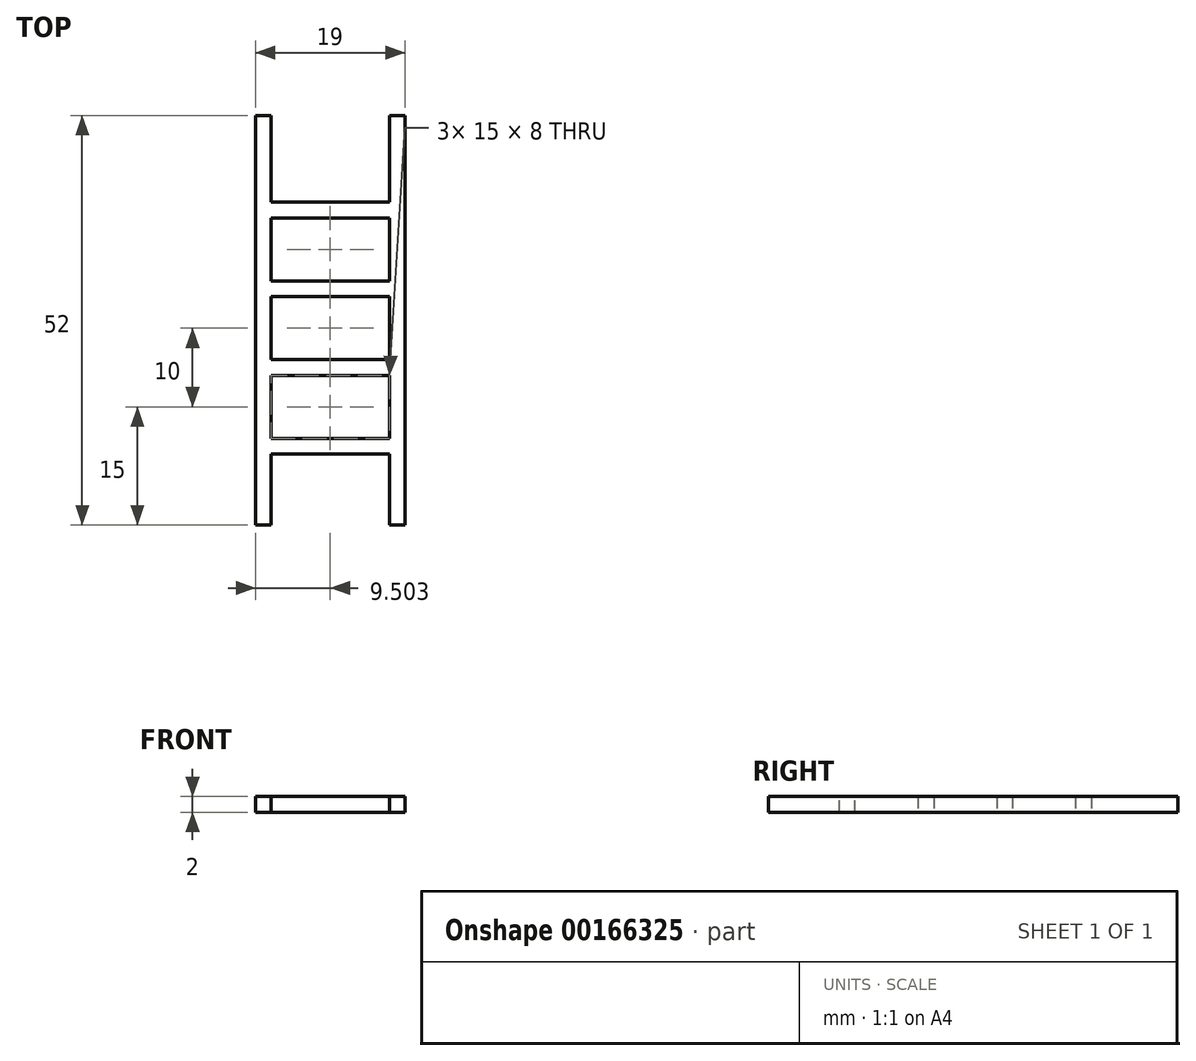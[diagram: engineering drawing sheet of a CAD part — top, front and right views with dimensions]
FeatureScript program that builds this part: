
annotation { "Feature Type Name" : "Feature", "Feature Type Description" : "" }
export const myFeature = defineFeature(function(context is Context, id is Id, definition is map)
    precondition{}
    {
        {
            var Q0;
            Q0=qCreatedBy(makeId("Front.planeOp"),FACE);
            var sketch = newSketch(context, id + "F0", { "sketchPlane" : qUnion([Q0])});
            skLineSegment(sketch, "E0.bottom", {"start": v(-30.22, 16.27) * mm, "end": v(-28.22, 16.27) * mm});
            skLineSegment(sketch, "E0.top", {"start": v(-30.22, 14.27) * mm, "end": v(-28.22, 14.27) * mm});
            skLineSegment(sketch, "E0.left", {"start": v(-30.22, 16.27) * mm, "end": v(-30.22, 14.27) * mm});
            skLineSegment(sketch, "E0.right", {"start": v(-28.22, 16.27) * mm, "end": v(-28.22, 14.27) * mm});
            skLineSegment(sketch, "E1.bottom", {"start": v(-13.22, 16.27) * mm, "end": v(-11.22, 16.27) * mm});
            skLineSegment(sketch, "E1.top", {"start": v(-13.22, 14.27) * mm, "end": v(-11.22, 14.27) * mm});
            skLineSegment(sketch, "E1.left", {"start": v(-13.22, 16.27) * mm, "end": v(-13.22, 14.27) * mm});
            skLineSegment(sketch, "E1.right", {"start": v(-11.22, 16.27) * mm, "end": v(-11.22, 14.27) * mm});
            skPoint(sketch, "E1.middle", {"position": v(-12.22, 15.27) * mm});
            skPoint(sketch, "E1.middle.positionSnap0", {"position": v(-28.22, 15.27) * mm});
            skPoint(sketch, "E1.centerSnap0", {"position": v(-28.22, 15.27) * mm});
            skSolve(sketch);
        }
        {
            var Q0;
            Q0=qSketchRegion(id+"F0",true);
            extrude(context, id + "F1", {"entities" : qUnion([Q0]), "depth" : 52 * mm});
        }
        {
            var Q0;
            Q0=makeQuery(id+"F1.opExtrude","SWEPT_FACE",FACE,{"disambiguationData":[OSD([sQuery(id+"F0.wireOp",EDGE,"E0.right")])]});
            var sketch = newSketch(context, id + "F2", { "sketchPlane" : qUnion([Q0])});
            skLineSegment(sketch, "E2.bottom", {"start": v(-41, 14.27) * mm, "end": v(-43, 14.27) * mm});
            skLineSegment(sketch, "E2.top", {"start": v(-41, 16.27) * mm, "end": v(-43, 16.27) * mm});
            skLineSegment(sketch, "E2.left", {"start": v(-41, 14.27) * mm, "end": v(-41, 16.27) * mm});
            skLineSegment(sketch, "E2.right", {"start": v(-43, 14.27) * mm, "end": v(-43, 16.27) * mm});
            skPoint(sketch, "E2.middle", {"position": v(-42, 15.27) * mm});
            skPoint(sketch, "E2.middle.positionSnap0", {"position": v(-52, 15.27) * mm});
            skPoint(sketch, "E2.centerSnap0", {"position": v(-52, 15.27) * mm});
            skLineSegment(sketch, "E3.bottom", {"start": v(-33, 16.27) * mm, "end": v(-31, 16.27) * mm});
            skLineSegment(sketch, "E3.top", {"start": v(-33, 14.27) * mm, "end": v(-31, 14.27) * mm});
            skLineSegment(sketch, "E3.left", {"start": v(-33, 16.27) * mm, "end": v(-33, 14.27) * mm});
            skLineSegment(sketch, "E3.right", {"start": v(-31, 16.27) * mm, "end": v(-31, 14.27) * mm});
            skPoint(sketch, "E3.middle", {"position": v(-32, 15.27) * mm});
            skPoint(sketch, "E3.middle.positionSnap0", {"position": v(-41, 15.27) * mm});
            skPoint(sketch, "E3.centerSnap0", {"position": v(-41, 15.27) * mm});
            skLineSegment(sketch, "E4.bottom", {"start": v(-23, 16.27) * mm, "end": v(-21, 16.27) * mm});
            skLineSegment(sketch, "E4.top", {"start": v(-23, 14.27) * mm, "end": v(-21, 14.27) * mm});
            skLineSegment(sketch, "E4.left", {"start": v(-23, 16.27) * mm, "end": v(-23, 14.27) * mm});
            skLineSegment(sketch, "E4.right", {"start": v(-21, 16.27) * mm, "end": v(-21, 14.27) * mm});
            skPoint(sketch, "E4.middle", {"position": v(-22, 15.27) * mm});
            skLineSegment(sketch, "E5.bottom", {"start": v(-13, 16.27) * mm, "end": v(-11, 16.27) * mm});
            skLineSegment(sketch, "E5.top", {"start": v(-13, 14.27) * mm, "end": v(-11, 14.27) * mm});
            skLineSegment(sketch, "E5.left", {"start": v(-13, 16.27) * mm, "end": v(-13, 14.27) * mm});
            skLineSegment(sketch, "E5.right", {"start": v(-11, 16.27) * mm, "end": v(-11, 14.27) * mm});
            skPoint(sketch, "E5.middle", {"position": v(-12, 15.27) * mm});
            skLineSegment(sketch, "E6.bottom", {"start": v(-11, 16.27) * mm, "end": v(-9, 16.27) * mm});
            skLineSegment(sketch, "E6.top", {"start": v(-11, 14.27) * mm, "end": v(-9, 14.27) * mm});
            skLineSegment(sketch, "E6.right", {"start": v(-9, 16.27) * mm, "end": v(-9, 14.27) * mm});
            skPoint(sketch, "E6.middle", {"position": v(-10, 15.27) * mm});
            skSolve(sketch);
        }
        {
            var Q0;
            Q0=makeQuery(id+"F2.imprint","IMPRINT",FACE,{"disambiguationData":[TD([[makeQuery(id+"F2.imprint","IMPRINT",EDGE,{"derivedFrom":sQuery(id+"F2.wireOp",EDGE,"E2.bottom")}),1.0]])]});
            var Q1;
            Q1=makeQuery(id+"F2.imprint","IMPRINT",FACE,{"disambiguationData":[TD([[makeQuery(id+"F2.imprint","IMPRINT",EDGE,{"derivedFrom":sQuery(id+"F2.wireOp",EDGE,"E3.bottom")}),-1.0]])]});
            var Q2;
            Q2=makeQuery(id+"F2.imprint","IMPRINT",FACE,{"disambiguationData":[TD([[makeQuery(id+"F2.imprint","IMPRINT",EDGE,{"derivedFrom":sQuery(id+"F2.wireOp",EDGE,"E4.bottom")}),-1.0]])]});
            var Q3;
            Q3=makeQuery(id+"F2.imprint","IMPRINT",FACE,{"disambiguationData":[TD([[makeQuery(id+"F2.imprint","IMPRINT",EDGE,{"derivedFrom":sQuery(id+"F2.wireOp",EDGE,"E5.bottom")}),-1.0]])]});
            extrude(context, id + "F3", {"entities" : qUnion([Q0, Q1, Q2, Q3]), "operationType" : NewBodyOperationType.ADD, "depth" : 15 * mm});
        }
    });
